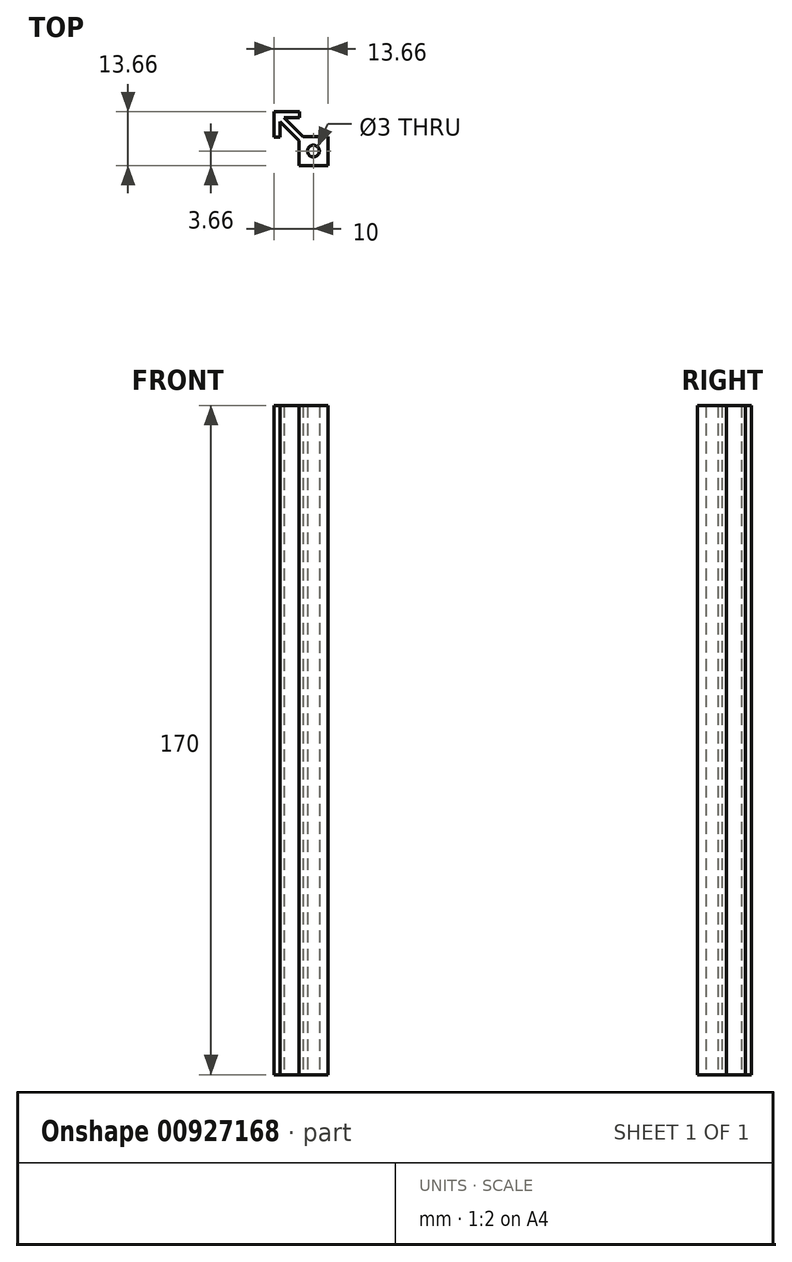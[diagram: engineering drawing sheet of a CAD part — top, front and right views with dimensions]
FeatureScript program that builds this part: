
annotation { "Feature Type Name" : "Feature", "Feature Type Description" : "" }
export const myFeature = defineFeature(function(context is Context, id is Id, definition is map)
    precondition{}
    {
        {
            var Q0;
            Q0=qCreatedBy(makeId("Top.planeOp"),FACE);
            var sketch = newSketch(context, id + "F0", { "sketchPlane" : qUnion([Q0])});
            skLineSegment(sketch, "E0.bottom", {"start": v(10, -10) * mm, "end": v(-10, -10) * mm, "construction": true});
            skLineSegment(sketch, "E0.left", {"start": v(10, -10) * mm, "end": v(10, 10) * mm, "construction": true});
            skPoint(sketch, "E0.middle", {"position": v(0, 0) * mm});
            skLineSegment(sketch, "E1.bottom", {"start": v(3.66, -3.66) * mm, "end": v(-3.66, -3.66) * mm});
            skLineSegment(sketch, "E1.top", {"start": v(3.66, 3.66) * mm, "end": v(-2.6, 3.66) * mm});
            skLineSegment(sketch, "E1.left", {"start": v(3.66, -3.66) * mm, "end": v(3.66, 3.66) * mm});
            skLineSegment(sketch, "E1.right", {"start": v(-3.66, -3.66) * mm, "end": v(-3.66, 2.6) * mm});
            skCircle(sketch, "E2", {"center": v(0, 0) * mm, "radius": 1.5 * mm});
            skLineSegment(sketch, "E3", {"start": v(-10, 10) * mm, "end": v(-10, 3.5) * mm});
            skLineSegment(sketch, "E4", {"start": v(-10, 3.5) * mm, "end": v(-8.5, 3.5) * mm});
            skLineSegment(sketch, "E5", {"start": v(-8.5, 3.5) * mm, "end": v(-8.5, 7.44) * mm});
            skLineSegment(sketch, "E6", {"start": v(-10, 10) * mm, "end": v(-3.5, 10) * mm});
            skLineSegment(sketch, "E7", {"start": v(-3.5, 10) * mm, "end": v(-3.5, 8.5) * mm});
            skLineSegment(sketch, "E8", {"start": v(-3.5, 8.5) * mm, "end": v(-7.44, 8.5) * mm});
            skLineSegment(sketch, "E9", {"start": v(-3.66, 2.6) * mm, "end": v(-8.5, 7.44) * mm});
            skLineSegment(sketch, "E10", {"start": v(-2.6, 3.66) * mm, "end": v(-7.44, 8.5) * mm});
            skLineSegment(sketch, "E11", {"start": v(10, 10) * mm, "end": v(-10, 10) * mm, "construction": true});
            skLineSegment(sketch, "E12", {"start": v(-10, -10) * mm, "end": v(-10, 10) * mm, "construction": true});
            skLineSegment(sketch, "E13", {"start": v(10, 0) * mm, "end": v(-10, 0) * mm, "construction": true});
            skLineSegment(sketch, "E14", {"start": v(-3.66, 2.6) * mm, "end": v(-3.66, 3.66) * mm, "construction": true});
            skLineSegment(sketch, "E15", {"start": v(-2.6, 3.66) * mm, "end": v(-3.66, 3.66) * mm, "construction": true});
            skLineSegment(sketch, "E16", {"start": v(-2.6, 3.66) * mm, "end": v(-3.66, 2.6) * mm});
            skLineSegment(sketch, "E17", {"start": v(-3.66, 3.66) * mm, "end": v(-3.13, 3.13) * mm, "construction": true});
            skSolve(sketch);
        }
        {
            var Q0;
            Q0=makeQuery(id+"F0.imprint","IMPRINT",FACE,{"disambiguationData":[TD([[makeQuery(id+"F0.imprint","IMPRINT",EDGE,{"derivedFrom":sQuery(id+"F0.wireOp",EDGE,"E1.bottom")}),-1.0]])]});
            var Q1;
            Q1=makeQuery(id+"F0.imprint","IMPRINT",FACE,{"disambiguationData":[TD([[makeQuery(id+"F0.imprint","IMPRINT",EDGE,{"derivedFrom":sQuery(id+"F0.wireOp",EDGE,"E3")}),1.0]])]});
            var Q2;
            Q2=makeQuery(id+"FoEG6zqP1uR5Ezh_0.3.F0.imprint","IMPRINT",FACE,{"disambiguationData":[TD([[makeQuery(id+"FoEG6zqP1uR5Ezh_0.3.F0.imprint","IMPRINT",EDGE,{"derivedFrom":sQuery(id+"FoEG6zqP1uR5Ezh_0.3.F0.wireOp",EDGE,"E3")}),1.0]])]});
            var Q3;
            Q3=makeQuery(id+"FoEG6zqP1uR5Ezh_0.2.F0.imprint","IMPRINT",FACE,{"disambiguationData":[TD([[makeQuery(id+"FoEG6zqP1uR5Ezh_0.2.F0.imprint","IMPRINT",EDGE,{"derivedFrom":sQuery(id+"FoEG6zqP1uR5Ezh_0.2.F0.wireOp",EDGE,"E3")}),1.0]])]});
            var Q4;
            Q4=makeQuery(id+"FoEG6zqP1uR5Ezh_0.1.F0.imprint","IMPRINT",FACE,{"disambiguationData":[TD([[makeQuery(id+"FoEG6zqP1uR5Ezh_0.1.F0.imprint","IMPRINT",EDGE,{"derivedFrom":sQuery(id+"FoEG6zqP1uR5Ezh_0.1.F0.wireOp",EDGE,"E3")}),1.0]])]});
            extrude(context, id + "F1", {"entities" : qUnion([Q0, Q1, Q2, Q3, Q4]), "depth" : 170 * mm, "offsetDistance" : 25 * mm});
        }
    });
